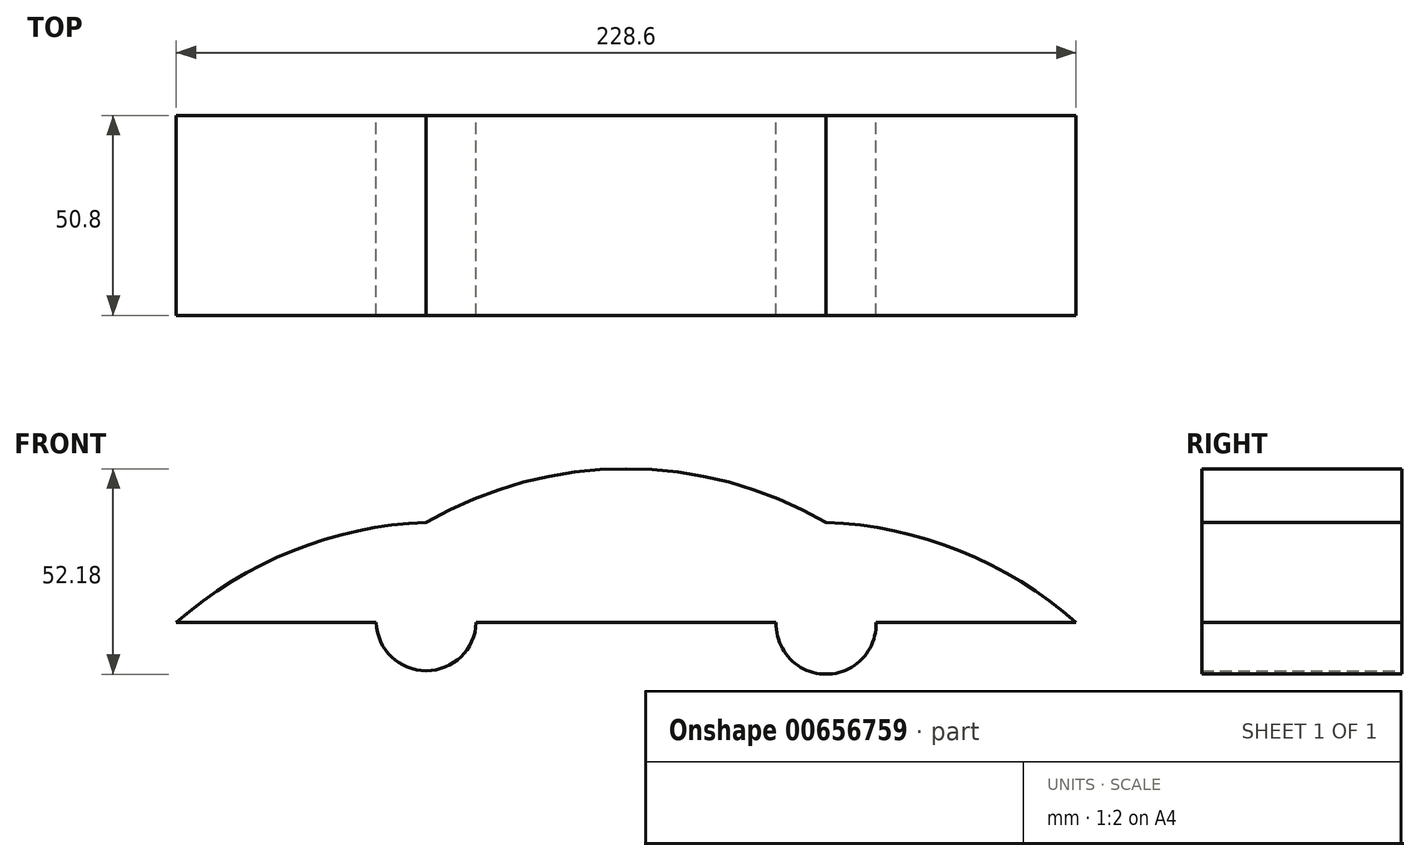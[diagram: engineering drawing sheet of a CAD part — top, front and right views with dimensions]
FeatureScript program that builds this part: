
annotation { "Feature Type Name" : "Feature", "Feature Type Description" : "" }
export const myFeature = defineFeature(function(context is Context, id is Id, definition is map)
    precondition{}
    {
        {
            var Q0;
            Q0=qCreatedBy(makeId("Front.planeOp"),FACE);
            var sketch = newSketch(context, id + "F0", { "sketchPlane" : qUnion([Q0])});
            skLineSegment(sketch, "E0", {"start": v(-70.98, 11.81) * mm, "end": v(-20.18, 11.81) * mm});
            skLineSegment(sketch, "E1", {"start": v(5.22, 11.81) * mm, "end": v(81.42, 11.81) * mm});
            skArc(sketch, "E2", {"start": v(5.22, 11.81) * mm, "mid": v(-7.48, 24.46) * mm, "end": v(-20.18, 11.81) * mm});
            skLineSegment(sketch, "E3", {"start": v(106.82, 11.81) * mm, "end": v(157.62, 11.81) * mm});
            skArc(sketch, "E4", {"start": v(106.82, 11.81) * mm, "mid": v(94.12, 24.37) * mm, "end": v(81.42, 11.81) * mm});
            skArc(sketch, "E5", {"start": v(-20.18, 11.81) * mm, "mid": v(-7.48, -0.42) * mm, "end": v(5.22, 11.81) * mm});
            skArc(sketch, "E6", {"start": v(81.42, 11.81) * mm, "mid": v(94.12, -1.28) * mm, "end": v(106.82, 11.81) * mm});
            skArc(sketch, "E7", {"start": v(-7.48, 37.29) * mm, "mid": v(-41.44, 30.05) * mm, "end": v(-70.98, 11.81) * mm});
            skPoint(sketch, "E7.startSnap0", {"position": v(-7.48, 24.46) * mm});
            skArc(sketch, "E8", {"start": v(94.12, 37.29) * mm, "mid": v(43.32, 50.9) * mm, "end": v(-7.48, 37.29) * mm});
            skPoint(sketch, "E8.startSnap0", {"position": v(94.12, 24.37) * mm});
            skArc(sketch, "E9", {"start": v(157.62, 11.81) * mm, "mid": v(128.08, 30.05) * mm, "end": v(94.12, 37.29) * mm});
            skSolve(sketch);
        }
        {
            var Q0;
            Q0=makeQuery(id+"F0.imprint","IMPRINT",FACE,{"disambiguationData":[TD([[makeQuery(id+"F0.imprint","IMPRINT",EDGE,{"derivedFrom":sQuery(id+"F0.wireOp",EDGE,"E0")}),1.0]])]});
            var Q1;
            Q1=makeQuery(id+"F0.imprint","IMPRINT",FACE,{"disambiguationData":[TD([[makeQuery(id+"F0.imprint","IMPRINT",EDGE,{"derivedFrom":sQuery(id+"F0.wireOp",EDGE,"E2")}),1.0]])]});
            var Q2;
            Q2=makeQuery(id+"F0.imprint","IMPRINT",FACE,{"disambiguationData":[TD([[makeQuery(id+"F0.imprint","IMPRINT",EDGE,{"derivedFrom":sQuery(id+"F0.wireOp",EDGE,"E4")}),1.0]])]});
            extrude(context, id + "F1", {"entities" : qUnion([Q0, Q1, Q2]), "depth" : 50.8 * mm, "offsetDistance" : 25.4 * mm});
        }
    });
